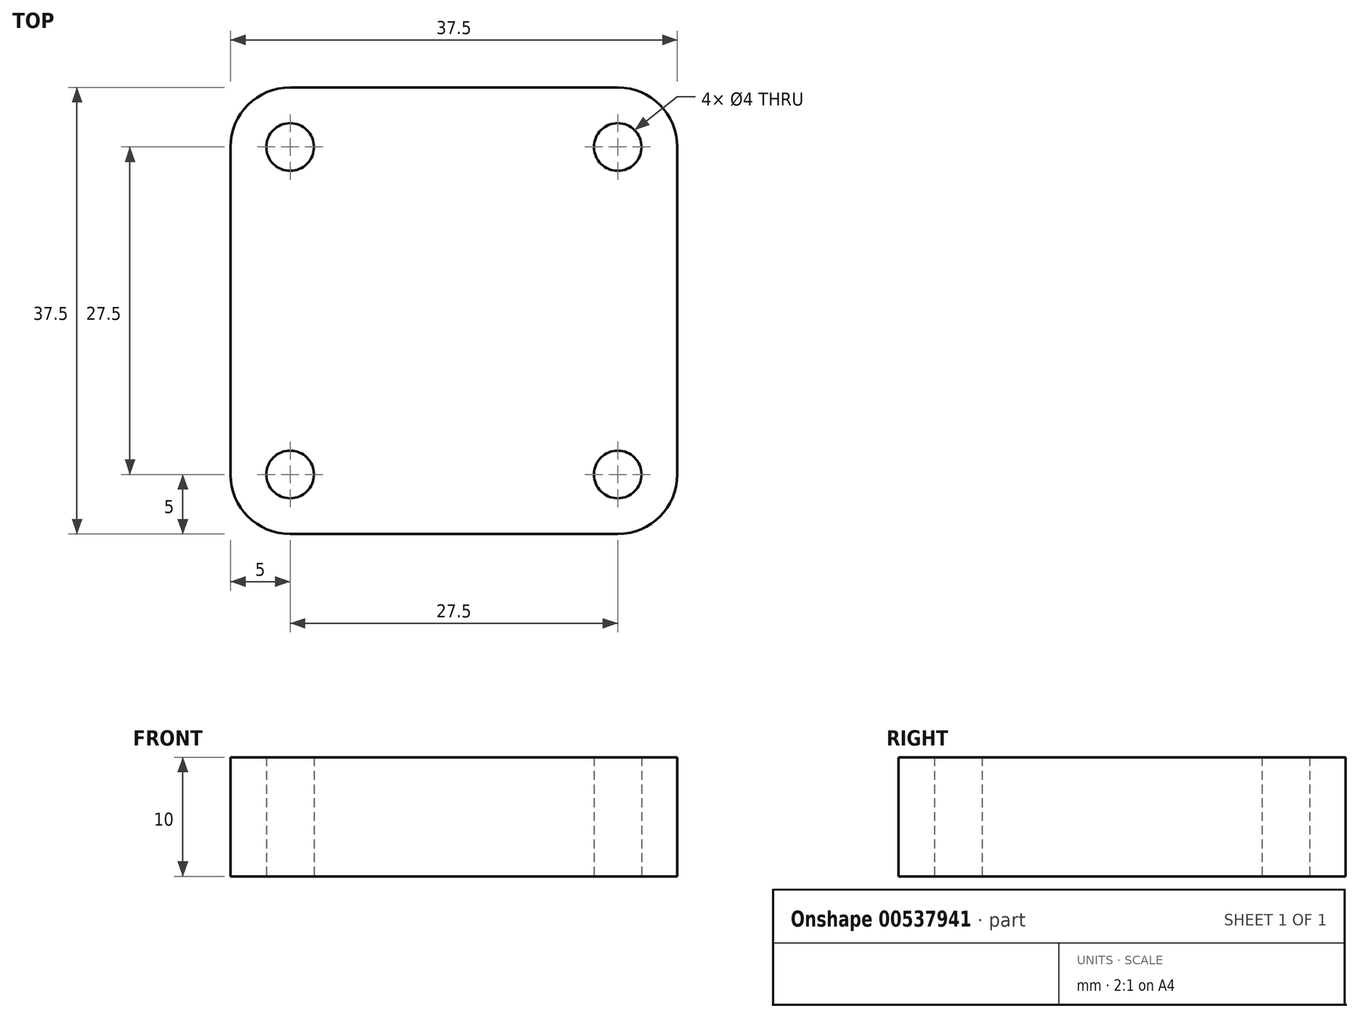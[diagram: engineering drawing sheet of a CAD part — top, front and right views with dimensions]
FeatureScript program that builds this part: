
annotation { "Feature Type Name" : "Feature", "Feature Type Description" : "" }
export const myFeature = defineFeature(function(context is Context, id is Id, definition is map)
    precondition{}
    {
        {
            var Q0;
            Q0=qCreatedBy(makeId("Top.planeOp"),FACE);
            var sketch = newSketch(context, id + "F0", { "sketchPlane" : qUnion([Q0])});
            skLineSegment(sketch, "E0.bottom", {"start": v(0, 0) * mm, "end": v(37.5, 0) * mm});
            skLineSegment(sketch, "E0.top", {"start": v(0, 37.5) * mm, "end": v(37.5, 37.5) * mm});
            skLineSegment(sketch, "E0.left", {"start": v(0, 0) * mm, "end": v(0, 37.5) * mm});
            skLineSegment(sketch, "E0.right", {"start": v(37.5, 0) * mm, "end": v(37.5, 37.5) * mm});
            skCircle(sketch, "E1", {"center": v(5, 5) * mm, "radius": 2 * mm});
            skCircle(sketch, "E2", {"center": v(5, 32.5) * mm, "radius": 2 * mm});
            skCircle(sketch, "E3", {"center": v(32.5, 32.5) * mm, "radius": 2 * mm});
            skCircle(sketch, "E4", {"center": v(32.5, 5) * mm, "radius": 2 * mm});
            skSolve(sketch);
        }
        {
            var Q0;
            Q0=makeQuery(id+"F0.imprint","IMPRINT",FACE,{"disambiguationData":[TD([[makeQuery(id+"F0.imprint","IMPRINT",EDGE,{"derivedFrom":sQuery(id+"F0.wireOp",EDGE,"E0.bottom")}),1.0]])]});
            extrude(context, id + "F1", {"entities" : qUnion([Q0]), "depth" : 10 * mm, "offsetDistance" : 25 * mm});
        }
        {
            var Q0;
            Q0=makeQuery(id+"F1.opExtrude","SWEPT_EDGE",EDGE,{"disambiguationData":[OSD([sQuery(id+"F0.wireOp",EDGE,"E0.bottom"),sQuery(id+"F0.wireOp",EDGE,"E0.right")])]});
            var Q1;
            Q1=makeQuery(id+"F1.opExtrude","SWEPT_EDGE",EDGE,{"disambiguationData":[OSD([sQuery(id+"F0.wireOp",EDGE,"E0.top"),sQuery(id+"F0.wireOp",EDGE,"E0.right")])]});
            var Q2;
            Q2=makeQuery(id+"F1.opExtrude","SWEPT_EDGE",EDGE,{"disambiguationData":[OSD([sQuery(id+"F0.wireOp",EDGE,"E0.top"),sQuery(id+"F0.wireOp",EDGE,"E0.left")])]});
            var Q3;
            Q3=makeQuery(id+"F1.opExtrude","SWEPT_EDGE",EDGE,{"disambiguationData":[OSD([sQuery(id+"F0.wireOp",EDGE,"E0.bottom"),sQuery(id+"F0.wireOp",EDGE,"E0.left")])]});
            fillet(context, id + "F2", {"entities" : qUnion([Q0, Q1, Q2, Q3]), "radius" : 5 * mm, "tangentPropagation" : true, "allowEdgeOverflow" : false});
        }
    });
